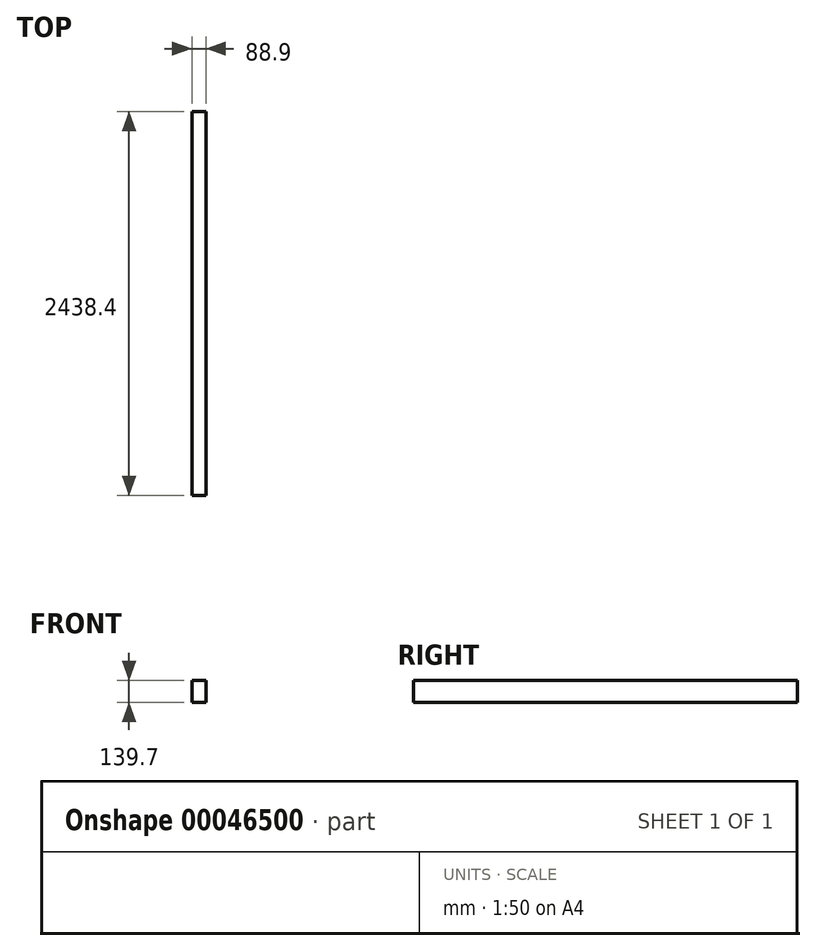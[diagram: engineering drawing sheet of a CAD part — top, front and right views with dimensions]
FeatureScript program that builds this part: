
annotation { "Feature Type Name" : "Feature", "Feature Type Description" : "" }
export const myFeature = defineFeature(function(context is Context, id is Id, definition is map)
    precondition{}
    {
        {
            var Q0;
            Q0=qCreatedBy(makeId("Front.planeOp"),FACE);
            var sketch = newSketch(context, id + "F0", { "sketchPlane" : qUnion([Q0])});
            skLineSegment(sketch, "E0", {"start": v(-44.45, -69.85) * mm, "end": v(-44.45, 69.85) * mm});
            skLineSegment(sketch, "E1", {"start": v(-44.45, 69.85) * mm, "end": v(44.45, 69.85) * mm});
            skLineSegment(sketch, "E2", {"start": v(44.45, 69.85) * mm, "end": v(44.45, -69.85) * mm});
            skLineSegment(sketch, "E3", {"start": v(44.45, -69.85) * mm, "end": v(-44.45, -69.85) * mm});
            skSolve(sketch);
        }
        {
            var Q0;
            Q0=makeQuery(id+"F0.imprint","IMPRINT",FACE,{"disambiguationData":[TD([[makeQuery(id+"F0.imprint","IMPRINT",EDGE,{"derivedFrom":sQuery(id+"F0.wireOp",EDGE,"E0")}),-1.0]])]});
            extrude(context, id + "F1", {"entities" : qUnion([Q0]), "depth" : 2438.4 * mm, "symmetric" : true});
        }
    });
